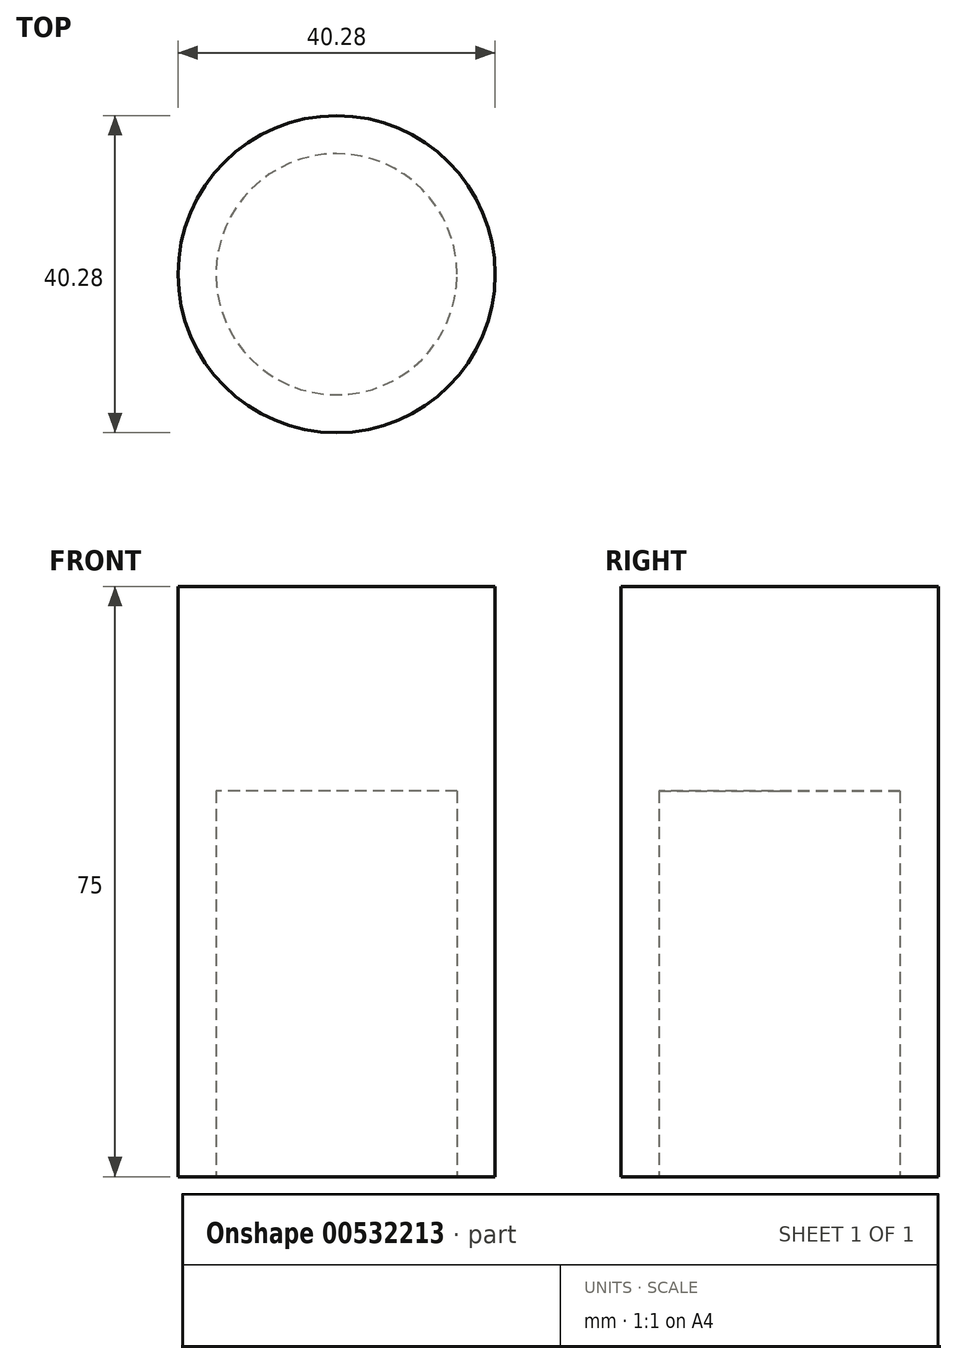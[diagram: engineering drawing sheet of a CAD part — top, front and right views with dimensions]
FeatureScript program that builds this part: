
annotation { "Feature Type Name" : "Feature", "Feature Type Description" : "" }
export const myFeature = defineFeature(function(context is Context, id is Id, definition is map)
    precondition{}
    {
        {
            var Q0;
            Q0=qCreatedBy(makeId("Top.planeOp"),FACE);
            var sketch = newSketch(context, id + "F0", { "sketchPlane" : qUnion([Q0])});
            skCircle(sketch, "E0", {"center": v(0, 0) * mm, "radius": 20.14 * mm});
            skSolve(sketch);
        }
        {
            var Q0;
            Q0 = qSketchRegion(id + "F0", true);
            extrude(context, id + "F1", {"entities" : qUnion([Q0]), "depth" : 50 * mm, "offsetDistance" : 25 * mm});
        }
        {
            var Q0;
            Q0=qCreatedBy(makeId("Top.planeOp"),FACE);
            var sketch = newSketch(context, id + "F2", { "sketchPlane" : qUnion([Q0])});
            skCircle(sketch, "E1", {"center": v(0, 0) * mm, "radius": 15.31 * mm});
            skSolve(sketch);
        }
        {
            var Q0;
            Q0 = qSketchRegion(id + "F2", true);
            extrude(context, id + "F3", {"entities" : qUnion([Q0]), "operationType" : NewBodyOperationType.REMOVE, "depth" : 49 * mm, "offsetDistance" : 25 * mm});
        }
        {
            var Q0;
            Q0=makeQuery(id+"F1.opExtrude","CAP_FACE",FACE,{"disambiguationData":[OSD([sQuery(id+"F0.wireOp",EDGE,"E0")])],"isStart":false});
            extrude(context, id + "F4", {"entities" : qUnion([Q0]), "operationType" : NewBodyOperationType.ADD, "depth" : 25 * mm, "offsetDistance" : 25 * mm});
        }
    });
